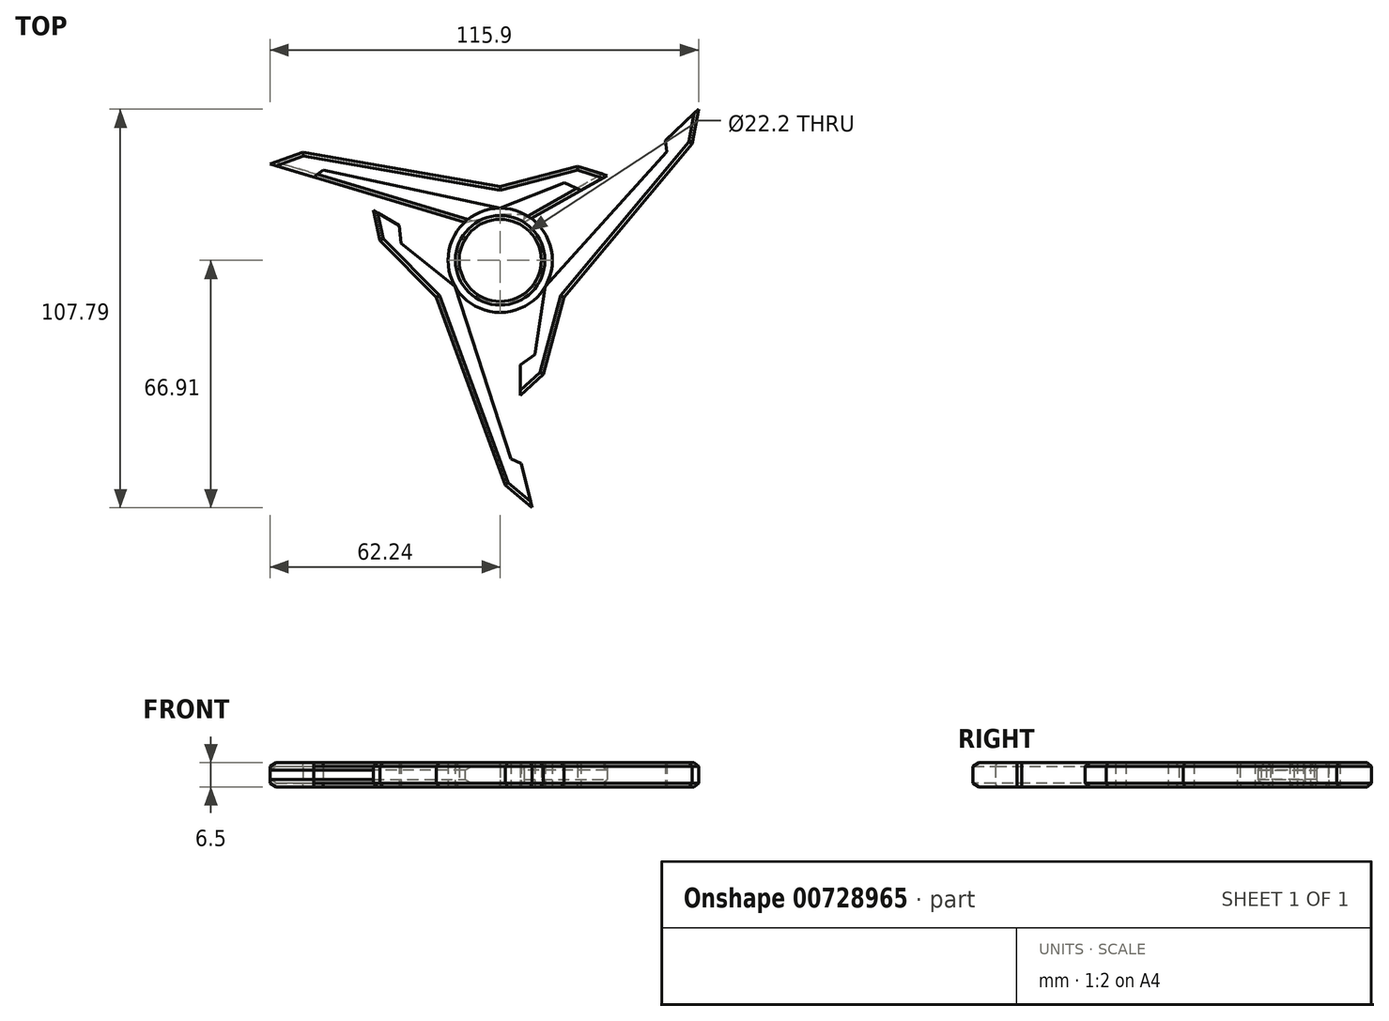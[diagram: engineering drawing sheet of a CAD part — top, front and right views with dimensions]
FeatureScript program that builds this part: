
annotation { "Feature Type Name" : "Feature", "Feature Type Description" : "" }
export const myFeature = defineFeature(function(context is Context, id is Id, definition is map)
    precondition{}
    {
        {
            var Q0;
            Q0=qCreatedBy(makeId("Top.planeOp"),FACE);
            var sketch = newSketch(context, id + "F0", { "sketchPlane" : qUnion([Q0])});
            skCircle(sketch, "E0", {"center": v(0, 0) * mm, "radius": 11.1 * mm});
            skCircle(sketch, "E1.0", {"center": v(0, 0) * mm, "radius": 14.1 * mm});
            skSolve(sketch);
        }
        {
            var Q0;
            Q0 = qSketchRegion(id + "F0", true);
            extrude(context, id + "F1", {"entities" : qUnion([Q0]), "depth" : 6.5 * mm, "offsetDistance" : 25 * mm});
        }
        {
            var Q0;
            Q0=qCreatedBy(makeId("Front.planeOp"),FACE);
            var sketch = newSketch(context, id + "F2", { "sketchPlane" : qUnion([Q0])});
            skLineSegment(sketch, "E2", {"start": v(0, 0) * mm, "end": v(0, 20.18) * mm});
            skSolve(sketch);
        }
        {
            var Q0;
            Q0=qCreatedBy(makeId("Top.planeOp"),FACE);
            cPlane(context, id + "F3", {"entities" : qUnion([Q0]), "cplaneType" : CPlaneType.OFFSET, "offset" : 1 * mm, "width" : 150 * mm, "height" : 150 * mm});
        }
        {
            var Q0;
            Q0=qCreatedBy(id+"F3.planeOp",FACE);
            var sketch = newSketch(context, id + "F4", { "sketchPlane" : qUnion([Q0])});
            skLineSegment(sketch, "E3", {"start": v(0, 12.43) * mm, "end": v(6.5, 12.43) * mm});
            skLineSegment(sketch, "E4", {"start": v(6.5, 12.43) * mm, "end": v(6.5, 10.23) * mm});
            skLineSegment(sketch, "E5", {"start": v(-9.55, 10.23) * mm, "end": v(0, 12.43) * mm});
            skLineSegment(sketch, "E6", {"start": v(6.5, 10.23) * mm, "end": v(28.91, 22.93) * mm});
            skLineSegment(sketch, "E7", {"start": v(-9.55, 10.23) * mm, "end": v(-62.24, 26.03) * mm});
            skLineSegment(sketch, "E8", {"start": v(-62.24, 26.03) * mm, "end": v(-53.31, 29.23) * mm});
            skLineSegment(sketch, "E9", {"start": v(-53.31, 29.23) * mm, "end": v(0, 19.99) * mm});
            skLineSegment(sketch, "E10", {"start": v(0, 19.99) * mm, "end": v(20.91, 25.48) * mm});
            skLineSegment(sketch, "E11", {"start": v(20.91, 25.48) * mm, "end": v(28.91, 22.93) * mm});
            skLineSegment(sketch, "E12", {"start": v(0, 12.43) * mm, "end": v(0, 0) * mm});
            skSolve(sketch);
        }
        {
            var Q0;
            Q0=makeQuery(id+"F4.imprint","IMPRINT",FACE,{"disambiguationData":[TD([[makeQuery(id+"F4.imprint","IMPRINT",EDGE,{"derivedFrom":sQuery(id+"F4.wireOp",EDGE,"E3")}),1.0]])]});
            extrude(context, id + "F5", {"entities" : qUnion([Q0]), "depth" : 4.5 * mm, "offsetDistance" : 25 * mm});
        }
        {
            var Q0;
            Q0=qCreatedBy(id+"F3.planeOp",FACE);
            cPlane(context, id + "F6", {"entities" : qUnion([Q0]), "cplaneType" : CPlaneType.OFFSET, "offset" : 1 * mm, "oppositeDirection" : true, "width" : 150 * mm, "height" : 150 * mm});
        }
        {
            var Q0;
            Q0=qCreatedBy(id+"F6.planeOp",FACE);
            var sketch = newSketch(context, id + "F7", { "sketchPlane" : qUnion([Q0])});
            skLineSegment(sketch, "E13", {"start": v(0, 12.43) * mm, "end": v(6.5, 12.43) * mm});
            skLineSegment(sketch, "E14", {"start": v(6.5, 12.43) * mm, "end": v(6.5, 10.23) * mm});
            skLineSegment(sketch, "E15", {"start": v(-9.55, 10.23) * mm, "end": v(0, 12.43) * mm});
            skLineSegment(sketch, "E16", {"start": v(6.5, 10.23) * mm, "end": v(28.92, 22.93) * mm});
            skLineSegment(sketch, "E17", {"start": v(-9.55, 10.23) * mm, "end": v(-62.24, 26.03) * mm});
            skLineSegment(sketch, "E18", {"start": v(-62.24, 26.03) * mm, "end": v(-53.31, 29.23) * mm});
            skLineSegment(sketch, "E19", {"start": v(-53.31, 29.23) * mm, "end": v(0, 19.99) * mm});
            skLineSegment(sketch, "E20", {"start": v(0, 19.99) * mm, "end": v(20.91, 25.48) * mm});
            skLineSegment(sketch, "E21", {"start": v(20.91, 25.48) * mm, "end": v(28.92, 22.93) * mm});
            skLineSegment(sketch, "E22", {"start": v(0, 12.43) * mm, "end": v(0, 0) * mm});
            skLineSegment(sketch, "E23", {"start": v(21.8, 18.9) * mm, "end": v(17.4, 20.93) * mm});
            skLineSegment(sketch, "E24", {"start": v(17.4, 20.93) * mm, "end": v(0, 14.1) * mm});
            skLineSegment(sketch, "E25", {"start": v(0, 14.1) * mm, "end": v(-47.96, 24.4) * mm});
            skLineSegment(sketch, "E26", {"start": v(-47.96, 24.4) * mm, "end": v(-50.42, 22.48) * mm});
            skSolve(sketch);
        }
        {
            var Q0;
            {var subQ0=sQuery(id+"F7.wireOp",EDGE,"E18");Q0=makeQuery(id+"F7.imprint","IMPRINT",FACE,{"disambiguationData":[TD([[makeQuery(id+"F7.imprint","IMPRINT",EDGE,{"derivedFrom":subQ0}),-1.0]])]});}
            extrude(context, id + "F8", {"entities" : qUnion([Q0]), "depth" : 6.5 * mm, "offsetDistance" : 25 * mm});
        }
        {
            var Q0;
            Q0=makeQuery(id+"F8.opExtrude","CAP_EDGE",EDGE,{"disambiguationData":[OSD([sQuery(id+"F7.wireOp",EDGE,"E19")])],"isStart":false});
            var Q1;
            Q1=makeQuery(id+"F8.opExtrude","CAP_EDGE",EDGE,{"disambiguationData":[OSD([sQuery(id+"F7.wireOp",EDGE,"E20")])],"isStart":false});
            var Q2;
            Q2=makeQuery(id+"F8.opExtrude","CAP_EDGE",EDGE,{"disambiguationData":[OSD([sQuery(id+"F7.wireOp",EDGE,"E21")])],"isStart":false});
            var Q3;
            Q3=makeQuery(id+"F8.opExtrude","CAP_EDGE",EDGE,{"disambiguationData":[OSD([sQuery(id+"F7.wireOp",EDGE,"E18")])],"isStart":false});
            var Q4;
            Q4=makeQuery(id+"F8.opExtrude","CAP_EDGE",EDGE,{"disambiguationData":[OSD([sQuery(id+"F7.wireOp",EDGE,"E21")])],"isStart":true});
            var Q5;
            Q5=makeQuery(id+"F8.opExtrude","CAP_EDGE",EDGE,{"disambiguationData":[OSD([sQuery(id+"F7.wireOp",EDGE,"E20")])],"isStart":true});
            var Q6;
            Q6=makeQuery(id+"F8.opExtrude","CAP_EDGE",EDGE,{"disambiguationData":[OSD([sQuery(id+"F7.wireOp",EDGE,"E19")])],"isStart":true});
            var Q7;
            Q7=makeQuery(id+"F8.opExtrude","CAP_EDGE",EDGE,{"disambiguationData":[OSD([sQuery(id+"F7.wireOp",EDGE,"E18")])],"isStart":true});
            var Q8;
            Q8=makeQuery(id+"F5.opExtrude","CAP_EDGE",EDGE,{"disambiguationData":[OSD([sQuery(id+"F4.wireOp",EDGE,"E7")])],"isStart":false});
            var Q9;
            Q9=makeQuery(id+"F5.opExtrude","CAP_EDGE",EDGE,{"disambiguationData":[OSD([sQuery(id+"F4.wireOp",EDGE,"E7")])],"isStart":true});
            var Q10;
            Q10=makeQuery(id+"F5.opExtrude","CAP_EDGE",EDGE,{"disambiguationData":[OSD([sQuery(id+"F4.wireOp",EDGE,"E6")])],"isStart":true});
            var Q11;
            Q11=makeQuery(id+"F5.opExtrude","CAP_EDGE",EDGE,{"disambiguationData":[OSD([sQuery(id+"F4.wireOp",EDGE,"E6")])],"isStart":false});
            chamfer(context, id + "F9", {"entities" : qUnion([Q0, Q1, Q2, Q3, Q4, Q5, Q6, Q7, Q8, Q9, Q10, Q11]), "width" : 1 * mm, "tangentPropagation" : true});
        }
        {
            var Q0;
            Q0=makeQuery(id+"F8.opExtrude","SWEPT_BODY",BODY,{"disambiguationData":[OSD([sQuery(id+"F7.wireOp",EDGE,"E16"),sQuery(id+"F7.wireOp",EDGE,"E17"),sQuery(id+"F7.wireOp",EDGE,"E18"),sQuery(id+"F7.wireOp",EDGE,"E19"),sQuery(id+"F7.wireOp",EDGE,"E20"),sQuery(id+"F7.wireOp",EDGE,"E21"),sQuery(id+"F7.wireOp",EDGE,"E23"),sQuery(id+"F7.wireOp",EDGE,"E24"),sQuery(id+"F7.wireOp",EDGE,"E25"),sQuery(id+"F7.wireOp",EDGE,"E26")])]});
            var Q1;
            Q1=makeQuery(id+"F1.opExtrude","SWEPT_FACE",FACE,{"disambiguationData":[OSD([sQuery(id+"F0.wireOp",EDGE,"E1.0")])]});
            circularPattern(context, id + "F10", {"entities" : qUnion([Q0]), "axis" : qUnion([Q1]), "angle" : 360 * degree, "instanceCount" : 3, "equalSpace" : true});
        }
        {
            var Q0;
            Q0=makeQuery(id+"F1.opExtrude","CAP_EDGE",EDGE,{"disambiguationData":[OSD([sQuery(id+"F0.wireOp",EDGE,"E0")])],"isStart":false});
            var Q1;
            Q1=makeQuery(id+"F1.opExtrude","SWEPT_FACE",FACE,{"disambiguationData":[OSD([sQuery(id+"F0.wireOp",EDGE,"E0")])]});
            chamfer(context, id + "F11", {"entities" : qUnion([Q0, Q1]), "width" : 1 * mm, "tangentPropagation" : true});
        }
    });
